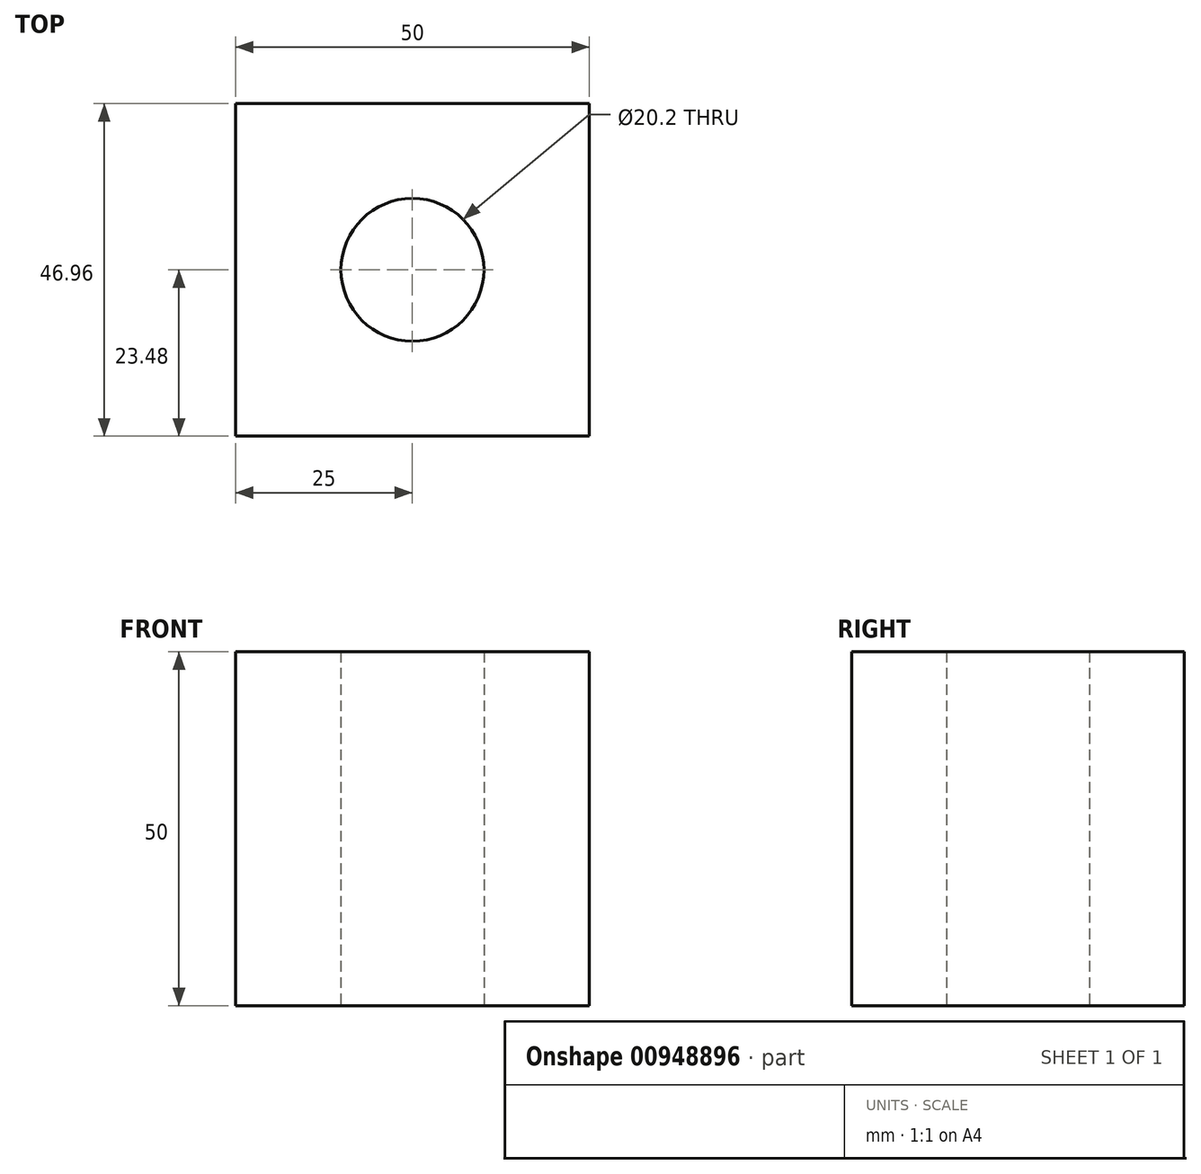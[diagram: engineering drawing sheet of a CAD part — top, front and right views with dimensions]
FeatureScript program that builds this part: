
annotation { "Feature Type Name" : "Feature", "Feature Type Description" : "" }
export const myFeature = defineFeature(function(context is Context, id is Id, definition is map)
    precondition{}
    {
        {
            var Q0;
            Q0=qCreatedBy(makeId("Top.planeOp"),FACE);
            var sketch = newSketch(context, id + "F0", { "sketchPlane" : qUnion([Q0])});
            skLineSegment(sketch, "E0.bottom", {"start": v(-25, 23.48) * mm, "end": v(25, 23.48) * mm});
            skLineSegment(sketch, "E0.top", {"start": v(-25, -23.48) * mm, "end": v(25, -23.48) * mm});
            skLineSegment(sketch, "E0.left", {"start": v(-25, 23.48) * mm, "end": v(-25, -23.48) * mm});
            skLineSegment(sketch, "E0.right", {"start": v(25, 23.48) * mm, "end": v(25, -23.48) * mm});
            skPoint(sketch, "E0.middle", {"position": v(0, 0) * mm});
            skCircle(sketch, "E1", {"center": v(0, 0) * mm, "radius": 10.1 * mm});
            skSolve(sketch);
        }
        {
            var Q0;
            Q0=makeQuery(id+"F0.imprint","IMPRINT",FACE,{"disambiguationData":[TD([[makeQuery(id+"F0.imprint","IMPRINT",EDGE,{"derivedFrom":sQuery(id+"F0.wireOp",EDGE,"E0.bottom")}),-1.0]])]});
            extrude(context, id + "F1", {"entities" : qUnion([Q0]), "depth" : 50 * mm, "offsetDistance" : 25 * mm});
        }
    });
